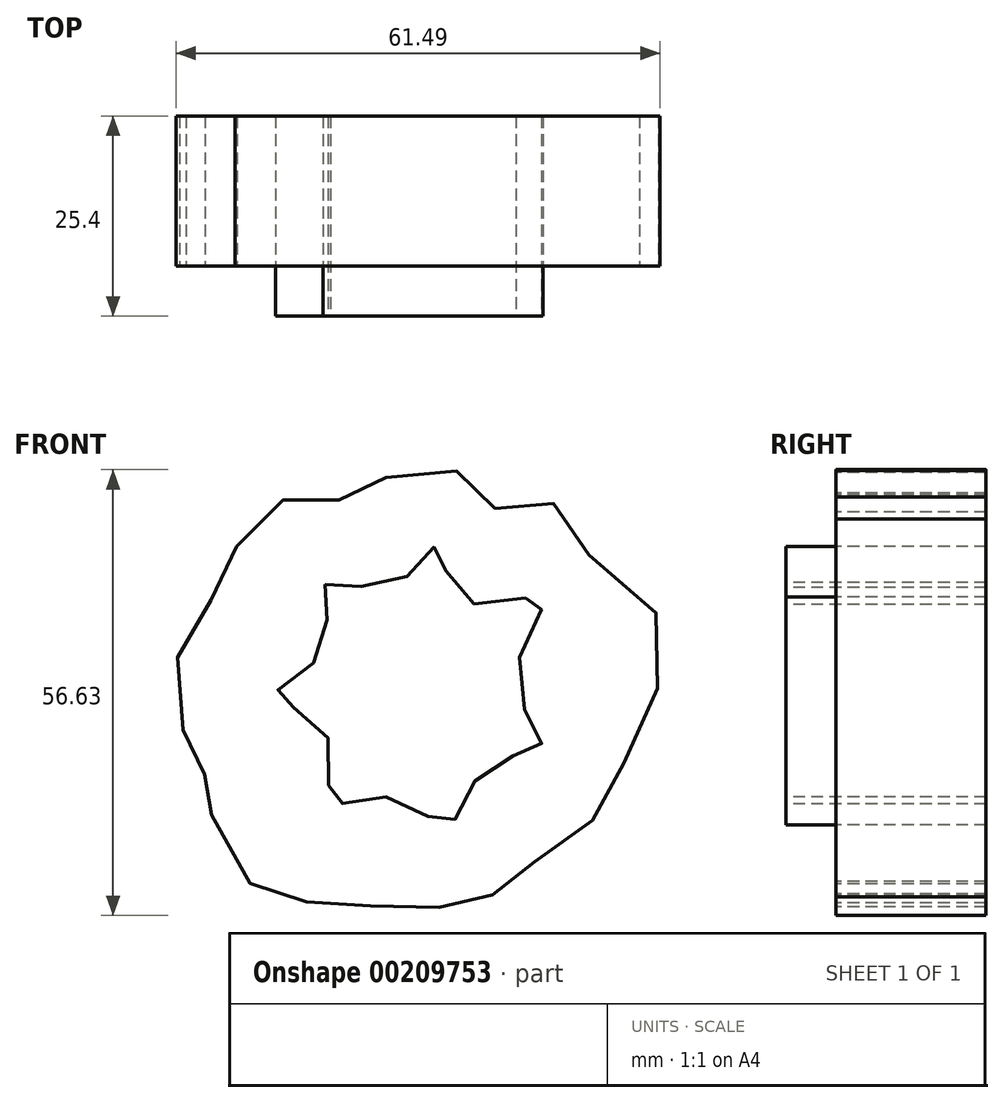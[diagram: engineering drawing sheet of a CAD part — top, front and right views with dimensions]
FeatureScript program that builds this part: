
annotation { "Feature Type Name" : "Feature", "Feature Type Description" : "" }
export const myFeature = defineFeature(function(context is Context, id is Id, definition is map)
    precondition{}
    {
        {
            var Q0;
            Q0=qCreatedBy(makeId("Front.planeOp"),FACE);
            var sketch = newSketch(context, id + "F0", { "sketchPlane" : qUnion([Q0])});
            skFitSpline(sketch, "E0", {"points": [v(-32.53, 37.81) * mm, v(-23.77, 37.81) * mm, v(-18.3, 42.64) * mm, v(-14.88, 35.82) * mm, v(-4.98, 36.05) * mm, v(-8.26, 25.78) * mm, v(-5.06, 17.41) * mm, v(-12.09, 14.5) * mm, v(-16.77, 7.35) * mm, v(-24.25, 10.75) * mm, v(-31.77, 10.27) * mm, v(-32.53, 19.17) * mm, v(-38.83, 23.82) * mm, v(-32.53, 29.78) * mm, v(-32.53, 37.81) * mm]});
            skLineSegment(sketch, "E1", {"start": v(-32.53, 37.81) * mm, "end": v(-29.53, 49.37) * mm});
            skLineSegment(sketch, "E2", {"start": v(-29.53, 49.37) * mm, "end": v(-18.3, 42.64) * mm});
            skLineSegment(sketch, "E3", {"start": v(-32.53, 37.81) * mm, "end": v(-47.6, 35.34) * mm});
            skLineSegment(sketch, "E4", {"start": v(-47.6, 35.34) * mm, "end": v(-38.83, 23.82) * mm});
            skLineSegment(sketch, "E5", {"start": v(-18.3, 42.64) * mm, "end": v(-9.33, 46.6) * mm});
            skLineSegment(sketch, "E6", {"start": v(-9.33, 46.6) * mm, "end": v(-4.98, 36.05) * mm});
            skLineSegment(sketch, "E7", {"start": v(-4.98, 36.05) * mm, "end": v(9.8, 23.82) * mm});
            skLineSegment(sketch, "E8", {"start": v(9.8, 23.82) * mm, "end": v(-5.06, 17.41) * mm});
            skLineSegment(sketch, "E9", {"start": v(-5.06, 17.41) * mm, "end": v(-1.88, 4.08) * mm});
            skLineSegment(sketch, "E10", {"start": v(-1.88, 4.08) * mm, "end": v(-16.77, 7.35) * mm});
            skLineSegment(sketch, "E11", {"start": v(-16.77, 7.35) * mm, "end": v(-26.12, -3.15) * mm});
            skLineSegment(sketch, "E12", {"start": v(-26.12, -3.15) * mm, "end": v(-31.77, 10.27) * mm});
            skLineSegment(sketch, "E13", {"start": v(-31.77, 10.27) * mm, "end": v(-50.15, 10.27) * mm});
            skLineSegment(sketch, "E14", {"start": v(-50.15, 10.27) * mm, "end": v(-38.83, 23.82) * mm});
            skLineSegment(sketch, "E15", {"start": v(-32.53, 37.81) * mm, "end": v(-21.87, 25.34) * mm});
            skLineSegment(sketch, "E16", {"start": v(-21.87, 25.34) * mm, "end": v(-18.3, 42.64) * mm});
            skLineSegment(sketch, "E17", {"start": v(-21.87, 25.34) * mm, "end": v(-4.98, 36.05) * mm});
            skLineSegment(sketch, "E18", {"start": v(-21.87, 25.34) * mm, "end": v(-5.06, 17.41) * mm});
            skLineSegment(sketch, "E19", {"start": v(-21.87, 25.34) * mm, "end": v(-16.77, 7.35) * mm});
            skLineSegment(sketch, "E20", {"start": v(-31.77, 10.27) * mm, "end": v(-21.87, 25.34) * mm});
            skLineSegment(sketch, "E21", {"start": v(-38.83, 23.82) * mm, "end": v(-21.87, 25.34) * mm});
            skLineSegment(sketch, "E22", {"start": v(-4.98, 36.05) * mm, "end": v(-2.32, 48.9) * mm});
            skLineSegment(sketch, "E23", {"start": v(-4.98, 36.05) * mm, "end": v(10.02, 35.82) * mm});
            skLineSegment(sketch, "E24", {"start": v(-18.3, 42.64) * mm, "end": v(-24.25, 52.04) * mm});
            skLineSegment(sketch, "E25", {"start": v(-24.25, 52.04) * mm, "end": v(-18.3, 42.64) * mm});
            skLineSegment(sketch, "E26", {"start": v(-18.3, 42.64) * mm, "end": v(-13.86, 52.04) * mm});
            skLineSegment(sketch, "E27", {"start": v(-43.77, 42.64) * mm, "end": v(-32.53, 37.81) * mm});
            skLineSegment(sketch, "E28", {"start": v(-32.53, 37.81) * mm, "end": v(-37.44, 48.9) * mm});
            skLineSegment(sketch, "E29", {"start": v(-37.44, 48.9) * mm, "end": v(-32.53, 37.81) * mm});
            skLineSegment(sketch, "E30", {"start": v(-51.43, 27.68) * mm, "end": v(-38.83, 23.82) * mm});
            skLineSegment(sketch, "E31", {"start": v(-51, 17.41) * mm, "end": v(-38.83, 23.82) * mm});
            skLineSegment(sketch, "E32", {"start": v(-42.28, 0) * mm, "end": v(-31.77, 10.27) * mm});
            skLineSegment(sketch, "E33", {"start": v(-34.84, -2.51) * mm, "end": v(-31.77, 10.27) * mm});
            skLineSegment(sketch, "E34", {"start": v(-16.77, -4.21) * mm, "end": v(-16.77, 7.35) * mm});
            skLineSegment(sketch, "E35", {"start": v(-8.26, -1.66) * mm, "end": v(-16.77, 7.35) * mm});
            skLineSegment(sketch, "E36", {"start": v(4.92, 10.27) * mm, "end": v(-5.06, 17.41) * mm});
            skFitSpline(sketch, "E37", {"points": [v(-43.77, 42.64) * mm, v(-39.3, 45.12) * mm, v(-37.44, 48.9) * mm, v(-33.14, 47.03) * mm, v(-29.53, 49.37) * mm, v(-26.12, 49.37) * mm, v(-24.25, 52.04) * mm, v(-18.68, 52.04) * mm, v(-13.86, 52.04) * mm, v(-12.1, 48.9) * mm, v(-9.33, 46.6) * mm, v(-5.29, 46.6) * mm, v(-2.32, 48.9) * mm, v(0, 42.64) * mm, v(10.02, 35.82) * mm, v(7.47, 30.66) * mm, v(9.8, 23.82) * mm, v(5.98, 17.9) * mm, v(4.92, 10.27) * mm, v(1.52, 7.9) * mm, v(-1.88, 4.08) * mm, v(-6.99, 1.74) * mm, v(-8.26, -1.66) * mm, v(-13.86, -1.66) * mm, v(-16.77, -4.21) * mm, v(-19.96, -1.66) * mm, v(-26.12, -3.15) * mm, v(-29.53, -1.66) * mm, v(-34.84, -2.51) * mm, v(-37.44, 0) * mm, v(-42.28, 0) * mm, v(-43.77, 6.42) * mm, v(-50.15, 10.27) * mm, v(-47.84, 13.03) * mm, v(-49.08, 15.14) * mm, v(-51, 17.41) * mm, v(-50.15, 21.3) * mm, v(-51.43, 27.68) * mm, v(-50.15, 30.66) * mm, v(-47.6, 35.34) * mm, v(-43.77, 38.74) * mm, v(-43.77, 42.64) * mm]});
            skSolve(sketch);
        }
        {
            var Q0;
            Q0=sQuery(id+"F0.wireOp",EDGE,"E0");
            extrude(context, id + "F1", {"bodyType" : ToolBodyType.SURFACE, "surfaceEntities" : qUnion([Q0]), "depth" : 25.4 * mm});
        }
        {
            var Q0;
            Q0=sQuery(id+"F0.wireOp",EDGE,"E0");
            extrude(context, id + "F2", {"bodyType" : ToolBodyType.SURFACE, "surfaceEntities" : qUnion([Q0]), "depth" : 25.4 * mm});
        }
        {
            var Q0;
            Q0=sQuery(id+"F0.wireOp",EDGE,"E37");
            extrude(context, id + "F3", {"bodyType" : ToolBodyType.SURFACE, "surfaceEntities" : qUnion([Q0]), "depth" : 19.05 * mm});
        }
    });
